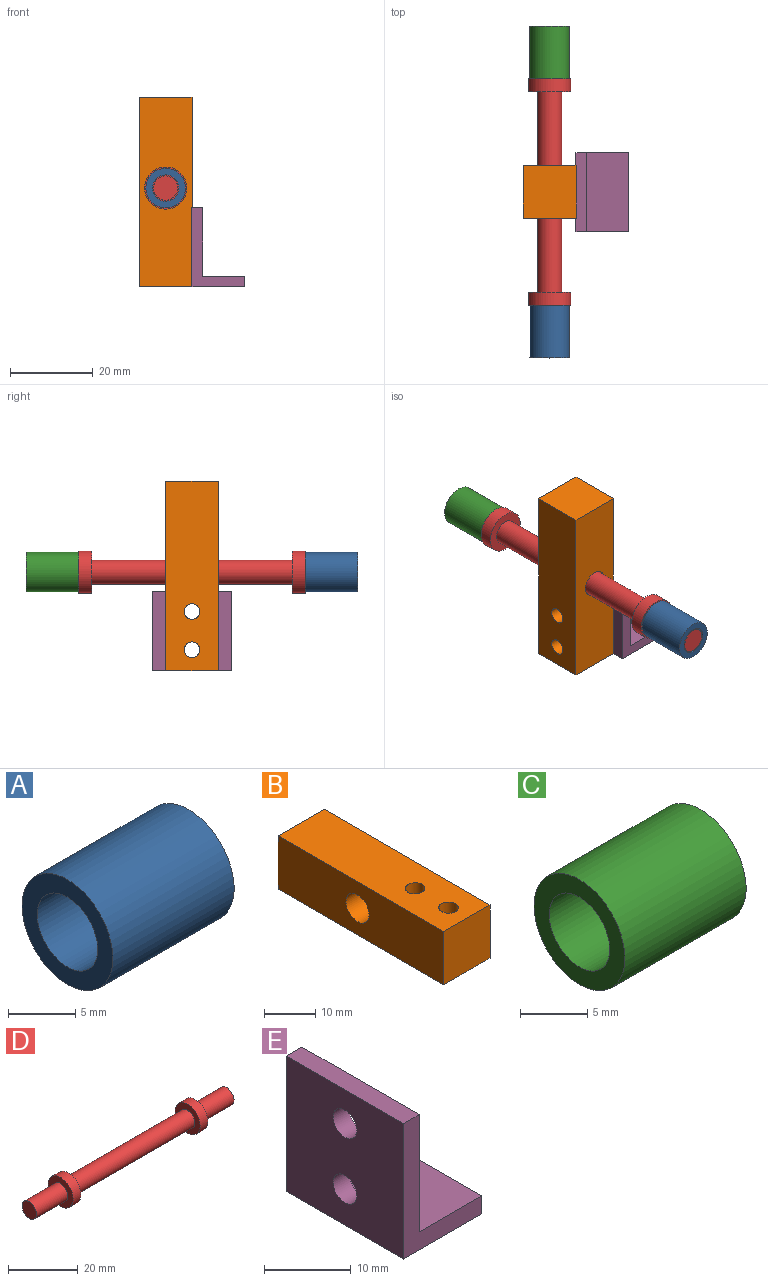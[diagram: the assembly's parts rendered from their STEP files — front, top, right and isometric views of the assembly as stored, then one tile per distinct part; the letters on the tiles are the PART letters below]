
ASSEMBLY  parts=5 mates=4
PART A: 4 faces, bbox 12.7x9.5x9.5 mm
  f0: cylinder r=3.17mm len=12.7mm, axis (-1,0,0), area 253.4mm2, adj f2,f3
  f1: cylinder r=4.76mm len=12.7mm, axis (-1,0,0), area 380mm2, adj f2,f3
  f2: plane 9.53x9.53mm, normal (1,0,0), area 39.6mm2, adj f0,f1
  f3: plane 9.53x9.53mm, normal (-1,0,0), area 39.6mm2, adj f0,f1
PART B: 9 faces, bbox 12.7x45.7x12.7 mm
  f0: plane 45.72x12.7mm, normal (1,0,0), area 549mm2, adj f1,f3,f4,f5,f8
  f1: plane 45.72x12.7mm, normal (0,0,1), area 557.8mm2, adj f0,f2,f4,f5,f6,f7
  f2: plane 45.72x12.7mm, normal (-1,0,0), area 549mm2, adj f1,f3,f4,f5,f8
  f3: plane 45.72x12.7mm, normal (0,0,-1), area 557.8mm2, adj f0,f2,f4,f5,f6,f7
  f4: plane 12.7x12.7mm, normal (0,-1,0), area 161.3mm2, adj f0,f1,f2,f3
  f5: plane 12.7x12.7mm, normal (0,1,0), area 161.3mm2, adj f0,f1,f2,f3
  f6: cylinder r=1.91mm len=12.7mm, axis (0,0,1), area 152mm2, adj f1,f3
  f7: cylinder r=1.91mm len=12.7mm, axis (0,0,1), area 152mm2, adj f1,f3
  f8: cylinder r=3.17mm len=12.7mm, axis (-1,0,0), area 253.4mm2, adj f0,f2
PART C: 4 faces, bbox 12.7x9.5x9.5 mm
  f0: cylinder r=4.76mm len=12.7mm, axis (-1,0,0), area 380mm2, adj f2,f3
  f1: cylinder r=3.17mm len=12.7mm, axis (-1,0,0), area 253.4mm2, adj f2,f3
  f2: plane 9.53x9.53mm, normal (1,0,0), area 39.6mm2, adj f0,f1
  f3: plane 9.53x9.53mm, normal (-1,0,0), area 39.6mm2, adj f0,f1
PART D: 11 faces, bbox 80x10.2x10.2 mm
  f0: cylinder r=2.92mm len=12.7mm, axis (-1,0,0), area 233.1mm2, adj f1,f4
  f1: plane 5.84x5.84mm, normal (-1,0,0), area 26.8mm2, adj f0
  f2: cylinder r=5.08mm len=10.16mm, axis (-1,0,0), area 101.3mm2, adj f3,f4
  f3: plane 10.16x10.16mm, normal (1,0,0), area 54.3mm2, adj f2,f5
  f4: plane 10.16x10.16mm, normal (-1,0,0), area 54.3mm2, adj f0,f2
  f5: cylinder r=2.92mm len=48.26mm, axis (-1,0,0), area 885.7mm2, adj f3,f9
  f6: cylinder r=2.92mm len=12.7mm, axis (1,0,0), area 233.1mm2, adj f7,f10
  f7: plane 5.84x5.84mm, normal (1,0,0), area 26.8mm2, adj f6
  f8: cylinder r=5.08mm len=10.16mm, axis (1,0,0), area 101.3mm2, adj f9,f10
  f9: plane 10.16x10.16mm, normal (-1,0,0), area 54.3mm2, adj f5,f8
  f10: plane 10.16x10.16mm, normal (1,0,0), area 54.3mm2, adj f6,f8
PART E: 10 faces, bbox 12.7x19.1x19.1 mm
  f0: plane 19.05x2.54mm, normal (1,0,0), area 48.4mm2, adj f1,f5,f6,f7
  f1: plane 19.05x10.16mm, normal (0,0,1), area 193.5mm2, adj f0,f2,f6,f7
  f2: plane 19.05x16.51mm, normal (1,0,0), area 291.7mm2, adj f1,f3,f6,f7,f8,f9
  f3: plane 19.05x2.54mm, normal (0,0,1), area 48.4mm2, adj f2,f4,f6,f7
  f4: plane 19.05x19.05mm, normal (-1,0,0), area 340.1mm2, adj f3,f5,f6,f7,f8,f9
  f5: plane 19.05x12.7mm, normal (0,0,-1), area 241.9mm2, adj f0,f4,f6,f7
  f6: plane 19.05x12.7mm, normal (0,-1,0), area 74.2mm2, adj f0,f1,f2,f3,f4,f5
  f7: plane 19.05x12.7mm, normal (0,1,0), area 74.2mm2, adj f0,f1,f2,f3,f4,f5
  f8: cylinder r=1.91mm len=3.81mm, axis (-1,0,0), area 30.4mm2, adj f2,f4
  f9: cylinder r=1.91mm len=3.81mm, axis (-1,0,0), area 30.4mm2, adj f2,f4
PLACE A rot(axis=(0,0,-1),90deg) t=(77.38,32.24,-15.59)mm
PLACE B rot(axis=(0.58,0.58,0.58),120deg) t=(53.9,59.54,48.98)mm
PLACE C rot(axis=(0.58,-0.58,-0.58),120deg) t=(96.56,99.55,67.38)mm
PLACE D rot(axis=(0,0,-1),90deg) t=(20.47,99.55,5.67)mm
PLACE E t=(38.28,69.07,12.8)mm
MATE revolute C.f0 <-> D.f0  axis (0,1,0) through (53.9,93.2,27.07)mm
MATE fastened B.f6 <-> E.f9  axis (1,0,0) through (60.25,59.54,17.55)mm
MATE revolute D.f0 <-> A.f0  axis (0,-1,0) through (53.9,25.89,27.07)mm
MATE fastened B.f8 <-> D.f0  axis (0,-1,0) through (53.9,59.54,27.07)mm
